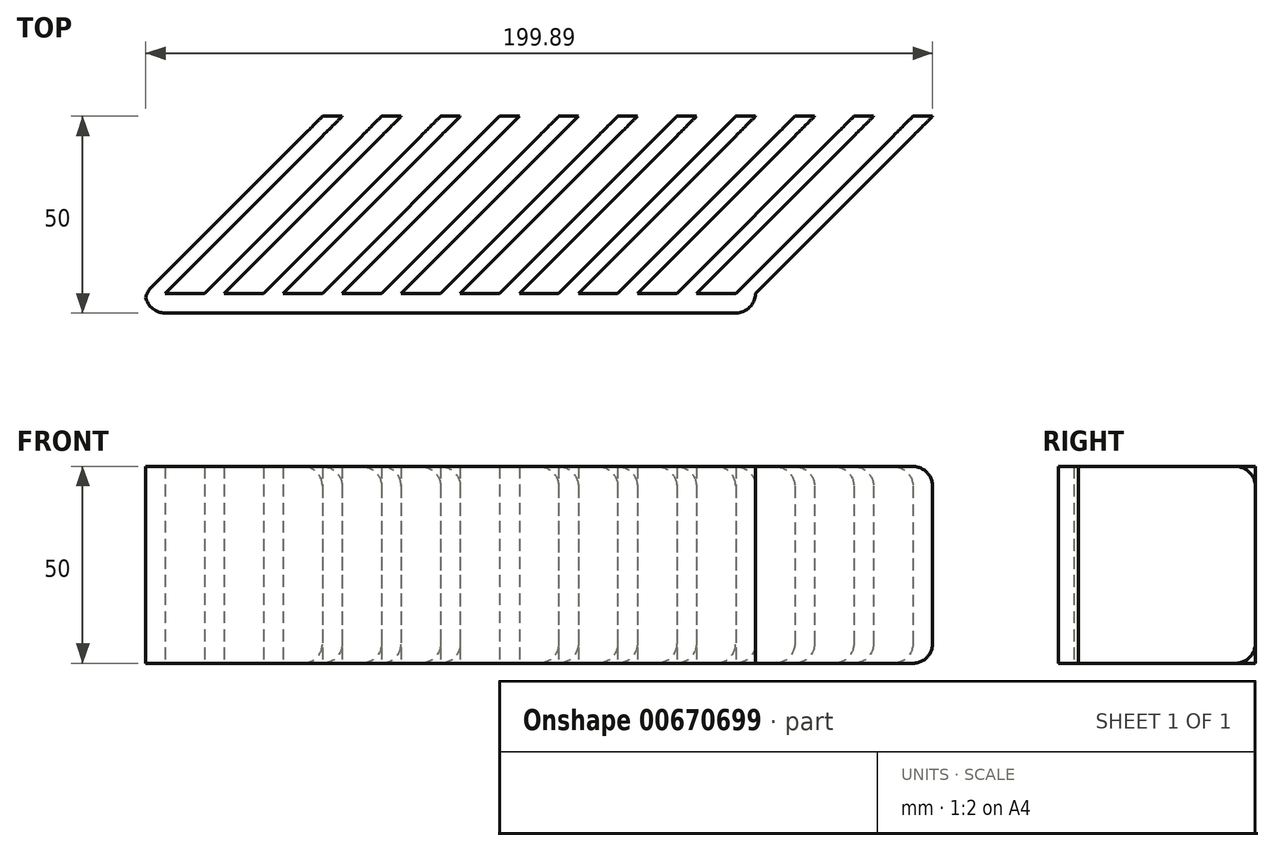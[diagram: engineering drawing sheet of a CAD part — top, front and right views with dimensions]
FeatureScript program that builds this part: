
annotation { "Feature Type Name" : "Feature", "Feature Type Description" : "" }
export const myFeature = defineFeature(function(context is Context, id is Id, definition is map)
    precondition{}
    {
        {
            var Q0;
            Q0=qCreatedBy(makeId("Top.planeOp"),FACE);
            var sketch = newSketch(context, id + "F0", { "sketchPlane" : qUnion([Q0])});
            skLineSegment(sketch, "E0", {"start": v(-69.74, -3.15) * mm, "end": v(-101.56, -34.96) * mm});
            skLineSegment(sketch, "E1", {"start": v(-101.56, -34.96) * mm, "end": v(-56.56, 10.04) * mm});
            skLineSegment(sketch, "E2", {"start": v(-96.56, -34.96) * mm, "end": v(-51.56, 10.04) * mm});
            skLineSegment(sketch, "E3", {"start": v(-86.56, -34.96) * mm, "end": v(-41.56, 10.04) * mm});
            skLineSegment(sketch, "E4", {"start": v(-86.56, -34.96) * mm, "end": v(-81.56, -34.96) * mm, "construction": true});
            skLineSegment(sketch, "E5", {"start": v(-36.56, 10.04) * mm, "end": v(-81.56, -34.96) * mm});
            skLineSegment(sketch, "E6", {"start": v(-71.56, -34.96) * mm, "end": v(-26.56, 10.04) * mm});
            skLineSegment(sketch, "E7", {"start": v(-66.56, -34.96) * mm, "end": v(-21.56, 10.04) * mm});
            skLineSegment(sketch, "E8", {"start": v(-56.56, -34.96) * mm, "end": v(-11.56, 10.04) * mm});
            skLineSegment(sketch, "E9", {"start": v(-51.56, -34.96) * mm, "end": v(-6.56, 10.04) * mm});
            skLineSegment(sketch, "E10", {"start": v(-56.56, 10.04) * mm, "end": v(-51.56, 10.04) * mm});
            skLineSegment(sketch, "E11", {"start": v(-41.56, 10.04) * mm, "end": v(-36.56, 10.04) * mm});
            skLineSegment(sketch, "E12", {"start": v(-26.56, 10.04) * mm, "end": v(-21.56, 10.04) * mm});
            skLineSegment(sketch, "E13", {"start": v(-11.56, 10.04) * mm, "end": v(-6.56, 10.04) * mm});
            skLineSegment(sketch, "E14", {"start": v(-41.56, -34.96) * mm, "end": v(3.44, 10.04) * mm});
            skLineSegment(sketch, "E15", {"start": v(-36.56, -34.96) * mm, "end": v(8.44, 10.04) * mm});
            skLineSegment(sketch, "E16", {"start": v(3.44, 10.04) * mm, "end": v(8.44, 10.04) * mm});
            skLineSegment(sketch, "E17", {"start": v(-26.56, -34.96) * mm, "end": v(18.44, 10.04) * mm});
            skLineSegment(sketch, "E18", {"start": v(-101.56, -34.96) * mm, "end": v(-101.56, -39.96) * mm});
            skLineSegment(sketch, "E19", {"start": v(-21.56, -34.96) * mm, "end": v(23.44, 10.04) * mm});
            skLineSegment(sketch, "E20", {"start": v(18.44, 10.04) * mm, "end": v(23.44, 10.04) * mm});
            skLineSegment(sketch, "E21", {"start": v(-11.56, -34.96) * mm, "end": v(33.44, 10.04) * mm});
            skLineSegment(sketch, "E22", {"start": v(-6.56, -34.96) * mm, "end": v(38.44, 10.04) * mm});
            skLineSegment(sketch, "E23", {"start": v(48.44, 10.04) * mm, "end": v(3.44, -34.96) * mm});
            skLineSegment(sketch, "E24", {"start": v(8.44, -34.96) * mm, "end": v(53.44, 10.04) * mm});
            skLineSegment(sketch, "E25", {"start": v(18.44, -34.96) * mm, "end": v(63.44, 10.04) * mm});
            skLineSegment(sketch, "E26", {"start": v(23.44, -34.96) * mm, "end": v(68.44, 10.04) * mm});
            skLineSegment(sketch, "E27", {"start": v(33.44, -34.96) * mm, "end": v(78.44, 10.04) * mm});
            skLineSegment(sketch, "E28", {"start": v(38.44, -34.96) * mm, "end": v(83.44, 10.04) * mm});
            skLineSegment(sketch, "E29", {"start": v(48.44, -34.96) * mm, "end": v(93.44, 10.04) * mm});
            skLineSegment(sketch, "E30", {"start": v(53.44, -34.96) * mm, "end": v(98.44, 10.04) * mm});
            skLineSegment(sketch, "E31", {"start": v(53.44, -34.96) * mm, "end": v(53.44, -39.96) * mm});
            skLineSegment(sketch, "E32", {"start": v(-101.56, -34.96) * mm, "end": v(53.44, -34.96) * mm});
            skLineSegment(sketch, "E33", {"start": v(-101.56, -39.96) * mm, "end": v(53.44, -39.96) * mm});
            skLineSegment(sketch, "E34", {"start": v(33.44, 10.04) * mm, "end": v(38.44, 10.04) * mm});
            skLineSegment(sketch, "E35", {"start": v(48.44, 10.04) * mm, "end": v(53.44, 10.04) * mm});
            skLineSegment(sketch, "E36", {"start": v(63.44, 10.04) * mm, "end": v(68.44, 10.04) * mm});
            skLineSegment(sketch, "E37", {"start": v(78.44, 10.04) * mm, "end": v(83.44, 10.04) * mm});
            skLineSegment(sketch, "E38", {"start": v(93.44, 10.04) * mm, "end": v(98.44, 10.04) * mm});
            skLineSegment(sketch, "E39", {"start": v(13.34, 4.93) * mm, "end": v(15.84, 2.43) * mm, "construction": true});
            skLineSegment(sketch, "E40", {"start": v(98.44, 10.04) * mm, "end": v(98.44, -41.88) * mm, "construction": true});
            skSolve(sketch);
        }
        {
            var Q0;
            Q0 = qSketchRegion(id + "F0", true);
            extrude(context, id + "F1", {"entities" : qUnion([Q0]), "endBound" : BoundingType.SYMMETRIC, "depth" : 50 * mm, "offsetDistance" : 25 * mm});
        }
        {
            var Q0;
            Q0=makeQuery(id+"F1.opExtrude","CAP_EDGE",EDGE,{"disambiguationData":[OSD([sQuery(id+"F0.wireOp",EDGE,"E10")])],"isStart":true});
            var Q1;
            Q1=makeQuery(id+"F1.opExtrude","CAP_EDGE",EDGE,{"disambiguationData":[OSD([sQuery(id+"F0.wireOp",EDGE,"E10")])],"isStart":false});
            var Q2;
            Q2=makeQuery(id+"F1.opExtrude","CAP_EDGE",EDGE,{"disambiguationData":[OSD([sQuery(id+"F0.wireOp",EDGE,"E11")])],"isStart":false});
            var Q3;
            Q3=makeQuery(id+"F1.opExtrude","CAP_EDGE",EDGE,{"disambiguationData":[OSD([sQuery(id+"F0.wireOp",EDGE,"E11")])],"isStart":true});
            var Q4;
            Q4=makeQuery(id+"F1.opExtrude","CAP_EDGE",EDGE,{"disambiguationData":[OSD([sQuery(id+"F0.wireOp",EDGE,"E12")])],"isStart":true});
            var Q5;
            Q5=makeQuery(id+"F1.opExtrude","CAP_EDGE",EDGE,{"disambiguationData":[OSD([sQuery(id+"F0.wireOp",EDGE,"E12")])],"isStart":false});
            var Q6;
            Q6=makeQuery(id+"F1.opExtrude","CAP_EDGE",EDGE,{"disambiguationData":[OSD([sQuery(id+"F0.wireOp",EDGE,"E13")])],"isStart":false});
            var Q7;
            Q7=makeQuery(id+"F1.opExtrude","CAP_EDGE",EDGE,{"disambiguationData":[OSD([sQuery(id+"F0.wireOp",EDGE,"E13")])],"isStart":true});
            var Q8;
            Q8=makeQuery(id+"F1.opExtrude","CAP_EDGE",EDGE,{"disambiguationData":[OSD([sQuery(id+"F0.wireOp",EDGE,"E16")])],"isStart":false});
            var Q9;
            Q9=makeQuery(id+"F1.opExtrude","CAP_EDGE",EDGE,{"disambiguationData":[OSD([sQuery(id+"F0.wireOp",EDGE,"E16")])],"isStart":true});
            var Q10;
            Q10=makeQuery(id+"F1.opExtrude","CAP_EDGE",EDGE,{"disambiguationData":[OSD([sQuery(id+"F0.wireOp",EDGE,"E20")])],"isStart":true});
            var Q11;
            Q11=makeQuery(id+"F1.opExtrude","CAP_EDGE",EDGE,{"disambiguationData":[OSD([sQuery(id+"F0.wireOp",EDGE,"E20")])],"isStart":false});
            var Q12;
            Q12=makeQuery(id+"F1.opExtrude","CAP_EDGE",EDGE,{"disambiguationData":[OSD([sQuery(id+"F0.wireOp",EDGE,"E34")])],"isStart":false});
            var Q13;
            Q13=makeQuery(id+"F1.opExtrude","CAP_EDGE",EDGE,{"disambiguationData":[OSD([sQuery(id+"F0.wireOp",EDGE,"E35")])],"isStart":false});
            var Q14;
            Q14=makeQuery(id+"F1.opExtrude","CAP_EDGE",EDGE,{"disambiguationData":[OSD([sQuery(id+"F0.wireOp",EDGE,"E36")])],"isStart":false});
            var Q15;
            Q15=makeQuery(id+"F1.opExtrude","CAP_EDGE",EDGE,{"disambiguationData":[OSD([sQuery(id+"F0.wireOp",EDGE,"E37")])],"isStart":false});
            var Q16;
            Q16=makeQuery(id+"F1.opExtrude","CAP_EDGE",EDGE,{"disambiguationData":[OSD([sQuery(id+"F0.wireOp",EDGE,"E38")])],"isStart":false});
            var Q17;
            Q17=makeQuery(id+"F1.opExtrude","CAP_EDGE",EDGE,{"disambiguationData":[OSD([sQuery(id+"F0.wireOp",EDGE,"E38")])],"isStart":true});
            var Q18;
            Q18=makeQuery(id+"F1.opExtrude","CAP_EDGE",EDGE,{"disambiguationData":[OSD([sQuery(id+"F0.wireOp",EDGE,"E37")])],"isStart":true});
            var Q19;
            Q19=makeQuery(id+"F1.opExtrude","CAP_EDGE",EDGE,{"disambiguationData":[OSD([sQuery(id+"F0.wireOp",EDGE,"E36")])],"isStart":true});
            var Q20;
            Q20=makeQuery(id+"F1.opExtrude","CAP_EDGE",EDGE,{"disambiguationData":[OSD([sQuery(id+"F0.wireOp",EDGE,"E35")])],"isStart":true});
            var Q21;
            Q21=makeQuery(id+"F1.opExtrude","CAP_EDGE",EDGE,{"disambiguationData":[OSD([sQuery(id+"F0.wireOp",EDGE,"E34")])],"isStart":true});
            var Q22;
            Q22=makeQuery(id+"F1.opExtrude","SWEPT_EDGE",EDGE,{"disambiguationData":[OSD([sQuery(id+"F0.wireOp",EDGE,"E1"),sQuery(id+"F0.wireOp",EDGE,"E18"),sQuery(id+"F0.wireOp",EDGE,"E32")])]});
            var Q23;
            Q23=makeQuery(id+"F1.opExtrude","SWEPT_EDGE",EDGE,{"disambiguationData":[OSD([sQuery(id+"F0.wireOp",EDGE,"E18"),sQuery(id+"F0.wireOp",EDGE,"E33")])]});
            var Q24;
            Q24=makeQuery(id+"F1.opExtrude","SWEPT_EDGE",EDGE,{"disambiguationData":[OSD([sQuery(id+"F0.wireOp",EDGE,"E31"),sQuery(id+"F0.wireOp",EDGE,"E33")])]});
            fillet(context, id + "F2", {"entities" : qUnion([Q0, Q1, Q2, Q3, Q4, Q5, Q6, Q7, Q8, Q9, Q10, Q11, Q12, Q13, Q14, Q15, Q16, Q17, Q18, Q19, Q20, Q21, Q22, Q23, Q24]), "radius" : 5 * mm, "tangentPropagation" : true, "allowEdgeOverflow" : false});
        }
    });
